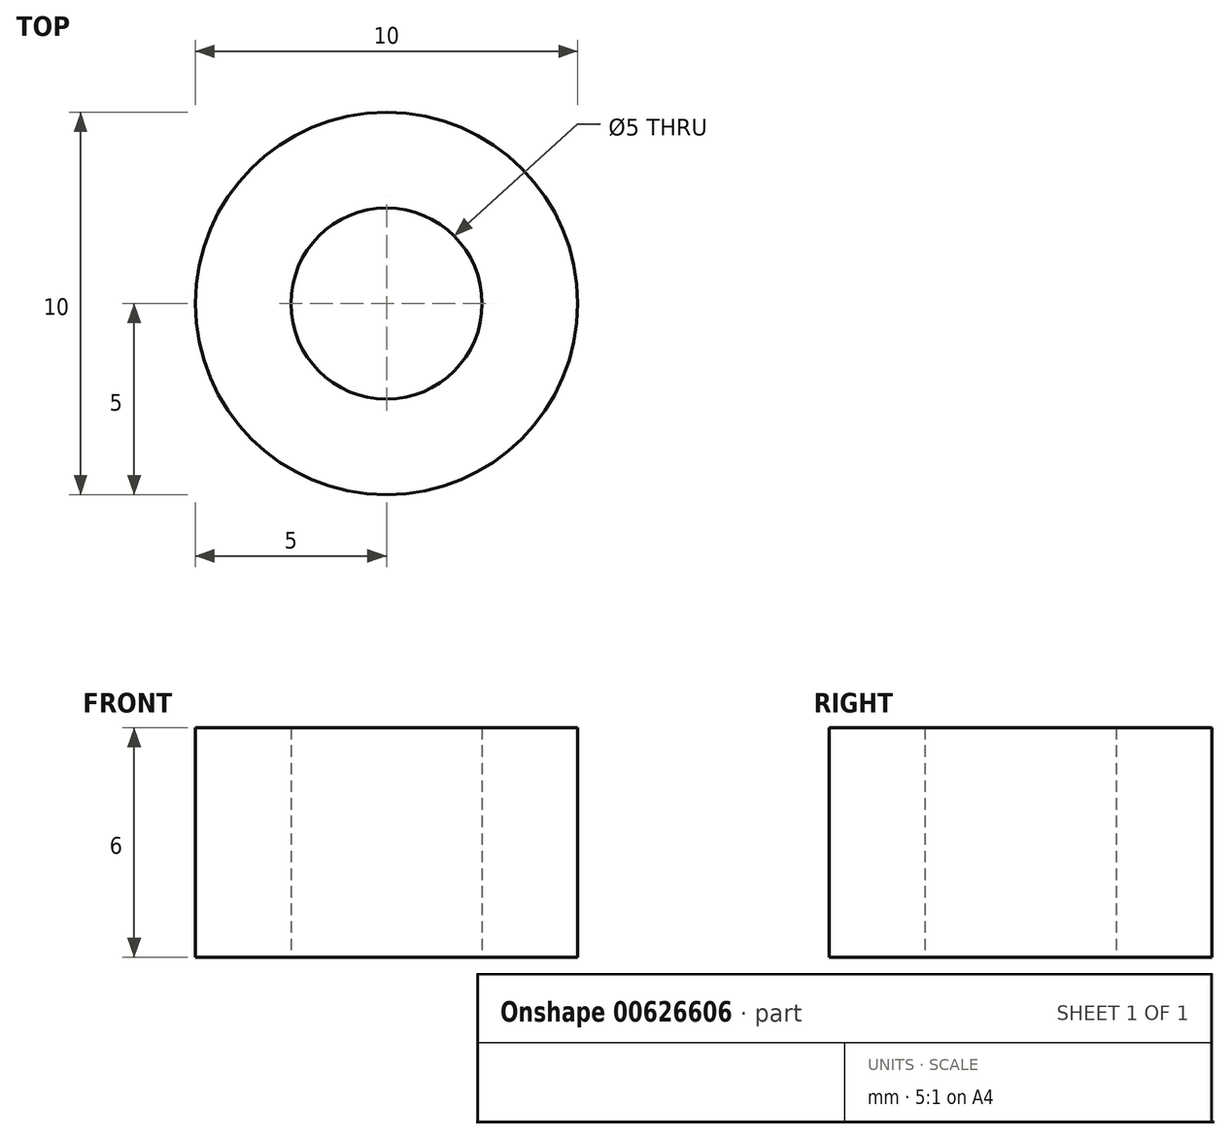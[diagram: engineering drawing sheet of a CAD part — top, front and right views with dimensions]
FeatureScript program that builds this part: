
annotation { "Feature Type Name" : "Feature", "Feature Type Description" : "" }
export const myFeature = defineFeature(function(context is Context, id is Id, definition is map)
    precondition{}
    {
        {
            var Q0;
            Q0=qCreatedBy(makeId("Top.planeOp"),FACE);
            var sketch = newSketch(context, id + "F0", { "sketchPlane" : qUnion([Q0])});
            skCircle(sketch, "E0", {"center": v(0, 0) * mm, "radius": 5 * mm});
            skCircle(sketch, "E1", {"center": v(0, 0) * mm, "radius": 2.5 * mm});
            skSolve(sketch);
        }
        {
            var Q0;
            Q0=makeQuery(id+"F0.imprint","IMPRINT",FACE,{"disambiguationData":[TD([[makeQuery(id+"F0.imprint","IMPRINT",EDGE,{"derivedFrom":sQuery(id+"F0.wireOp",EDGE,"E0")}),1.0]])]});
            extrude(context, id + "F1", {"entities" : qUnion([Q0]), "offsetDistance" : 25 * mm, "depth" : 6 * mm});
        }
    });
